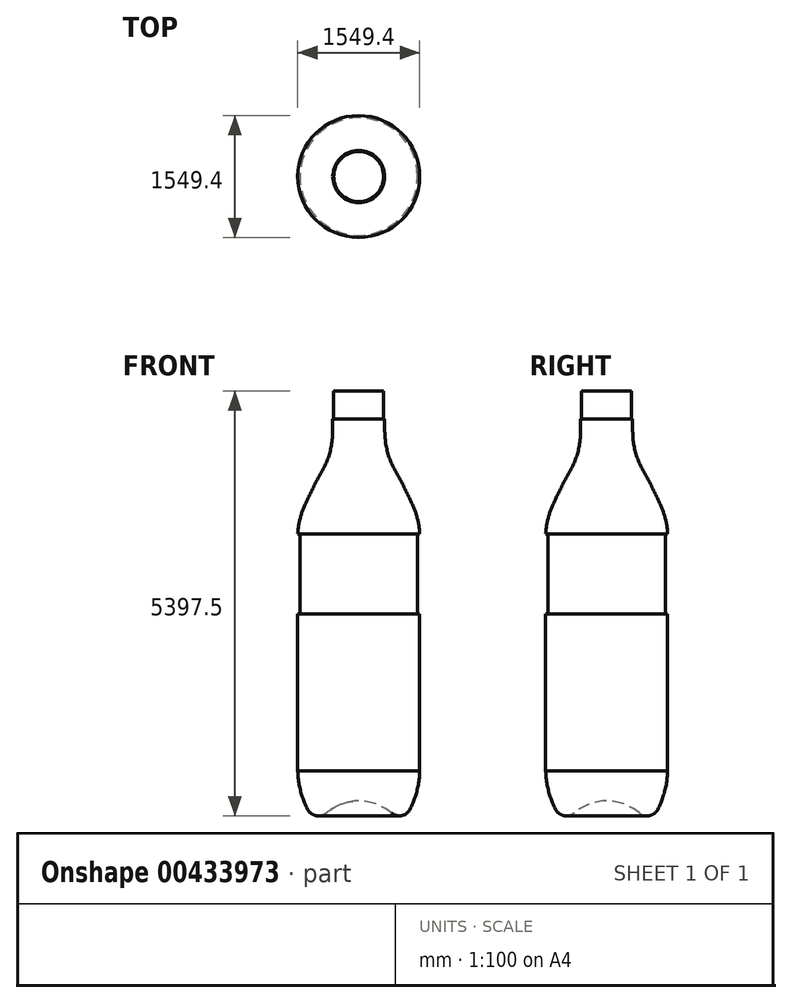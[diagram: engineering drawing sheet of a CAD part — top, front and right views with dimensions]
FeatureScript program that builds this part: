
annotation { "Feature Type Name" : "Feature", "Feature Type Description" : "" }
export const myFeature = defineFeature(function(context is Context, id is Id, definition is map)
    precondition{}
    {
        {
            var Q0;
            Q0=qCreatedBy(makeId("Front.planeOp"),FACE);
            var sketch = newSketch(context, id + "F0", { "sketchPlane" : qUnion([Q0])});
            skLineSegment(sketch, "E0", {"start": v(0, 0) * mm, "end": v(-317.5, 0) * mm});
            skLineSegment(sketch, "E1", {"start": v(-317.5, 0) * mm, "end": v(-317.5, -355.6) * mm});
            skLineSegment(sketch, "E2", {"start": v(-317.5, -355.6) * mm, "end": v(-330.2, -355.6) * mm});
            skLineSegment(sketch, "E3", {"start": v(-330.2, -355.6) * mm, "end": v(-330.2, -508) * mm});
            skArc(sketch, "E4", {"start": v(-462.44, -1009.22) * mm, "mid": v(-363.82, -767.18) * mm, "end": v(-330.2, -508) * mm});
            skArc(sketch, "E5", {"start": v(-462.44, -1009.22) * mm, "mid": v(-581.58, -1232.03) * mm, "end": v(-689.5, -1460.5) * mm});
            skArc(sketch, "E6", {"start": v(-689.5, -1460.5) * mm, "mid": v(-748.05, -1633.44) * mm, "end": v(-774.7, -1814.07) * mm});
            skLineSegment(sketch, "E7", {"start": v(0, 0) * mm, "end": v(0, -1460.5) * mm});
            skLineSegment(sketch, "E8", {"start": v(0, 0) * mm, "end": v(0, -5397.5) * mm});
            skLineSegment(sketch, "E9", {"start": v(0, -5397.5) * mm, "end": v(-774.7, -5397.5) * mm});
            skLineSegment(sketch, "E10", {"start": v(-774.7, -5397.5) * mm, "end": v(-774.7, -4762.5) * mm});
            skLineSegment(sketch, "E11", {"start": v(-774.7, -4762.5) * mm, "end": v(-774.7, -2830.07) * mm});
            skLineSegment(sketch, "E12", {"start": v(-774.7, -2830.07) * mm, "end": v(-746.76, -2830.07) * mm});
            skLineSegment(sketch, "E13", {"start": v(-746.76, -2830.07) * mm, "end": v(-746.76, -1814.07) * mm});
            skLineSegment(sketch, "E14", {"start": v(-746.76, -1814.07) * mm, "end": v(-774.7, -1814.07) * mm});
            skLineSegment(sketch, "E15", {"start": v(0, -5397.5) * mm, "end": v(0, -5207) * mm});
            skArc(sketch, "E16", {"start": v(0, -5207) * mm, "mid": v(-220.86, -5246.64) * mm, "end": v(-414.13, -5360.63) * mm});
            skLineSegment(sketch, "E17", {"start": v(0, -5207) * mm, "end": v(397.99, -5207) * mm});
            skArc(sketch, "E18", {"start": v(-649.13, -5314.65) * mm, "mid": v(-542.79, -5394.66) * mm, "end": v(-414.13, -5360.63) * mm});
            skArc(sketch, "E19", {"start": v(-774.7, -4762.5) * mm, "mid": v(-746.65, -5046.48) * mm, "end": v(-649.13, -5314.65) * mm});
            skSolve(sketch);
        }
        {
            var Q0;
            {var subQ1=sQuery(id+"F0.wireOp",EDGE,"E0");Q0=makeQuery(id+"F0.imprint","IMPRINT",FACE,{"disambiguationData":[TD([[makeQuery(id+"F0.imprint","IMPRINT",EDGE,{"derivedFrom":subQ1}),1.0]])]});}
            var Q1;
            Q1=sQuery(id+"F0.wireOp",EDGE,"E8");
            revolve(context, id + "F1", {"entities" : qUnion([Q0]), "axis" : qUnion([Q1]), "revolveType" : RevolveType.FULL});
        }
    });
